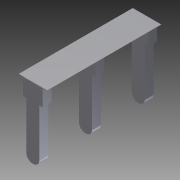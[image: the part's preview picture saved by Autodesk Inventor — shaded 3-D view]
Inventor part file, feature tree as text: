
AUTODESK INVENTOR PART (.ipt)
format: ipt  version: 2011 SP1 (Build 150282100, 282)  size: 112,128 bytes
history: native  units: in
note: dims shown in document units (in); Inventor stores cm internally (conversion verified against a paired STEP export)
features: extrude x4, sketch x4
ambient origin geometry x8: Origin, YZ Plane, XZ Plane, XY Plane, X Axis, Y Axis, Z Axis, Center Point
bodies: Solid1 (feature_tree), body_right_vert_XY (feature_tree), body_right_vert_YZ (feature_tree), body_right_vert_ZX (feature_tree), body_right_vert_X (feature_tree), body_right_vert_Y (feature_tree), body_right_vert_Z (feature_tree), body_right_vert_Center (feature_tree), body_straight_XY (feature_tree), body_straight_YZ (feature_tree), body_straight_ZX (feature_tree), body_straight_X (feature_tree), body_straight_Y (feature_tree), body_straight_Z (feature_tree), body_straight_Center (feature_tree)
feature tree (8):
  extrude  "Extrusion1"  Depth=0.031in TaperAngle=0.0deg
  extrude  "Extrusion2"  Depth=0.031in TaperAngle=0.0deg
  extrude  "Extrusion3"  [1 undecoded]
  extrude  "Extrusion4"  [1 undecoded]
  sketch  "Sketch_44"
  sketch  "Sketch_2"  dims[d0=0.001in d1=0.0in d2=0.031in d3=0.0in]
  sketch  "Sketch_3"  dims[d4=0.031in d5=0.0in d6=0.031in d7=0.0in]
  sketch  "Sketch_4"
note: 2 required parameter values undecoded (feature->parameter linkage not recoverable at this tier; creation-order binding heuristic only, values carry confidence <= 0.55)
